# Revit family: RM-22
name_source: partatom
category: Plumbing Fixtures
revit_build: Autodesk Revit 2014 (Build: 20130308_1515(x64)
units: mm (PartAtom-declared; Revit-internal decimal feet)

## types (1)
- RM-22
    CW Connection = Yes
    Certification = http://www.helvex.com.mx
    Chrome = Brass Chromed
    Description = Nuva Handheld Shower System With Slide Bar
    Documentation = http://www.helvex.com.mx
    Features = Medium and High Pressure Showerhead; Adjustable Slide; Fixed Stream
    HW Connection = Yes
    Inlet Threads = ½" - 14 NPT
    Instructive = http://www.helvex.com.mx
    Manufacturer = Helvex
    Max. Water Flow = 2.6 gal/min
    Max. Working Pressure = 85.3 psi
    Min. Water Flow = 0.7 gal/min
    Min. Working Pressure = 14.2 psi
    Model = RM-22
    Plastic Showerhead = Rubber
    Satin = Brass Satin
    Type Comments = Hand Held Shower Systems
    URL = http://www.helvex.com.mx

## geometry (parser evidence)
native form markers: Sweep x1
no freeform markers — native parametric forms only
